# Revit family: M_冷卻塔 - 閉合電路 - 逆流 - 11-62 kW
name_source: partatom
category: Attrezzatura meccanica
revit_build: Autodesk Revit 2017 (Build: 20160109_1515(x64)
units: mm (PartAtom-declared; Revit-internal decimal feet)

## family parameters
Basato su piano di lavoro = No
Condiviso = No
Numero OmniClass = 23.75.10.37.11
Punto di calcolo locali = No
Quota connettore circolare = Usa raggio
Sempre verticale = Sì
Taglio con vuoti quando caricato = No
Tipo di parte = Normale
Titolo OmniClass = Mechanical-Draft Cooling Towers

## types (13) — shared parameters
冷卻水半徑 = 50 mm
冷卻水直徑 = 100 mm
塔材料 = <Per categoria>
排水管半徑 = 50 mm
排水管直徑 = 100 mm
極數 = 3
補給水半徑 = 25 mm
補給水直徑 = 50 mm
負載分類 = 冷卻
電壓 = 460 V

## per-type parameters (varying)
| type | C1 偏移 1 | 可見 1 | 可見 2 | 塔長度 | 塔高度 | 表面負載 | 距離 1 | 長度 1 | 長度 2 | 風機數 | 馬達 HP | 馬達長度 |
| 27 kW | 580 mm  [stored 1.90289 ft] | No | Sì | 2720 mm  [stored 8.92388 ft] | 2430 mm  [stored 7.97244 ft] | 6890 VA | 495 mm  [stored 1.62402 ft] | 330 mm | 907 mm | 2 | 11 | 380 mm |
| 30 kW | 580 mm  [stored 1.90289 ft] | No | Sì | 3650 mm  [stored 11.9751 ft] | 2240 mm  [stored 7.34908 ft] | 7200 VA | 495 mm  [stored 1.62402 ft] | 380 mm | 1217 mm | 2 | 11.5 | 485 mm  [stored 1.59121 ft] |
| 31 kW | 580 mm  [stored 1.90289 ft] | No | Sì | 2720 mm  [stored 8.92388 ft] | 2620 mm  [stored 8.5958 ft] | 6890 VA | 495 mm  [stored 1.62402 ft] | 330 mm | 907 mm | 2 | 11 | 380 mm |
| 36 kW | 580 mm  [stored 1.90289 ft] | No | Sì | 3650 mm  [stored 11.9751 ft] | 2430 mm  [stored 7.97244 ft] | 10300 VA | 495 mm  [stored 1.62402 ft] | 380 mm | 1217 mm | 2 | 16.5 | 485 mm  [stored 1.59121 ft] |
| 41 kW | 580 mm  [stored 1.90289 ft] | No | Sì | 3650 mm  [stored 11.9751 ft] | 2620 mm  [stored 8.5958 ft] | 10300 VA | 495 mm  [stored 1.62402 ft] | 380 mm | 1217 mm | 2 | 16.5 | 485 mm  [stored 1.59121 ft] |
| 45 kW | 580 mm  [stored 1.90289 ft] | Sì | Sì | 5485 mm  [stored 17.9954 ft] | 2240 mm  [stored 7.34908 ft] | 10700 VA | 875 mm  [stored 2.87073 ft] | 300 mm | 1828 mm | 3 | 17 | 485 mm  [stored 1.59121 ft] |
| 55 kW | 580 mm  [stored 1.90289 ft] | Sì | Sì | 5485 mm  [stored 17.9954 ft] | 2430 mm  [stored 7.97244 ft] | 13800 VA | 875 mm  [stored 2.87073 ft] | 300 mm | 1828 mm | 3 | 22 | 485 mm  [stored 1.59121 ft] |
| 62 kW | 580 mm  [stored 1.90289 ft] | Sì | Sì | 5485 mm  [stored 17.9954 ft] | 2620 mm  [stored 8.5958 ft] | 1380000 VA | 875 mm  [stored 2.87073 ft] | 300 mm | 1828 mm | 3 | 22 | 485 mm  [stored 1.59121 ft] |
| 11 kW | 580 mm  [stored 1.90289 ft] | Sì | No | 1825 mm  [stored 5.98753 ft] | 2050 mm  [stored 6.72572 ft] | 3600 VA | 300 mm | 330 mm | 608 mm | 1 | 5.75 | 385 mm  [stored 1.26312 ft] |
| 15 kW | 600 mm | Sì | No | 1825 mm  [stored 5.98753 ft] | 2240 mm  [stored 7.34908 ft] | 3600 VA | 300 mm | 330 mm | 608 mm | 1 | 5.75 | 380 mm |
| 18 kW | 630 mm  [stored 2.06693 ft] | Sì | No | 1825 mm  [stored 5.98753 ft] | 2430 mm  [stored 7.97244 ft] | 3600 VA | 300 mm | 330 mm | 608 mm | 1 | 5.75 | 380 mm |
| 20 kW | 660 mm | Sì | No | 1825 mm  [stored 5.98753 ft] | 2620 mm  [stored 8.5958 ft] | 5170 VA | 300 mm | 330 mm | 608 mm | 1 | 8.25 | 380 mm |
| 22 kW | 580 mm  [stored 1.90289 ft] | No | Sì | 2725 mm  [stored 8.94029 ft] | 2240 mm  [stored 7.34908 ft] | 5330 VA | 495 mm  [stored 1.62402 ft] | 330 mm | 908 mm | 2 | 8.5 | 380 mm |

note: [stored X ft] marks values corroborated as IEEE doubles in the binary element streams (Revit-internal decimal feet)
